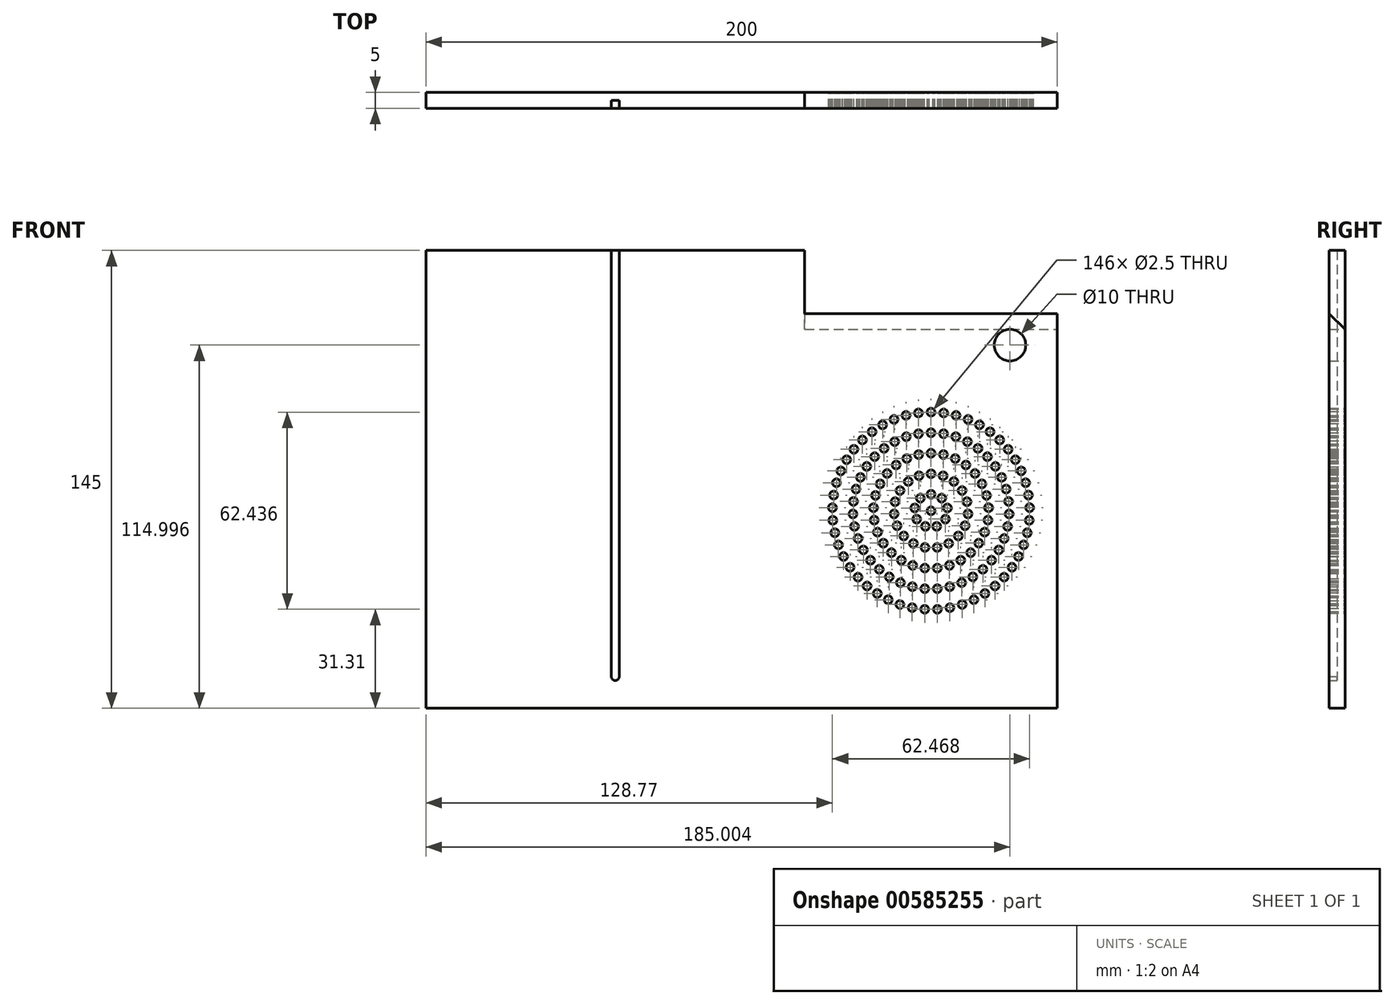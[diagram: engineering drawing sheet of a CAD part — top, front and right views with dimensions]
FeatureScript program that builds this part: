
annotation { "Feature Type Name" : "Feature", "Feature Type Description" : "" }
export const myFeature = defineFeature(function(context is Context, id is Id, definition is map)
    precondition{}
    {
        {
            var Q0;
            Q0=qCreatedBy(makeId("Front.planeOp"),FACE);
            var sketch = newSketch(context, id + "F0", { "sketchPlane" : qUnion([Q0])});
            skLineSegment(sketch, "E0", {"start": v(-78.93, 75.1) * mm, "end": v(1.07, 75.1) * mm});
            skLineSegment(sketch, "E1", {"start": v(1.07, 75.1) * mm, "end": v(1.07, -49.9) * mm});
            skLineSegment(sketch, "E2", {"start": v(-78.93, 75.1) * mm, "end": v(-78.93, 95.1) * mm});
            skLineSegment(sketch, "E3", {"start": v(-198.93, 95.1) * mm, "end": v(-198.93, -49.9) * mm});
            skLineSegment(sketch, "E4", {"start": v(-198.93, -49.9) * mm, "end": v(1.07, -49.9) * mm});
            skLineSegment(sketch, "E5", {"start": v(-198.93, 95.1) * mm, "end": v(-140.18, 95.1) * mm});
            skLineSegment(sketch, "E6", {"start": v(-140.18, 95.1) * mm, "end": v(-137.68, 95.1) * mm});
            skLineSegment(sketch, "E7", {"start": v(-137.68, 95.1) * mm, "end": v(-78.93, 95.1) * mm});
            skLineSegment(sketch, "E8", {"start": v(-140.18, 95.1) * mm, "end": v(-140.18, -39.9) * mm});
            skLineSegment(sketch, "E9", {"start": v(-137.68, 95.1) * mm, "end": v(-137.68, -39.9) * mm});
            skArc(sketch, "E10", {"start": v(-140.18, -39.9) * mm, "mid": v(-138.88, -41.14) * mm, "end": v(-137.68, -39.8) * mm});
            skLineSegment(sketch, "E11", {"start": v(-78.93, 75.1) * mm, "end": v(-78.93, -49.9) * mm});
            skPoint(sketch, "E12.endSnap0", {"position": v(-78.93, 12.6) * mm});
            skCircle(sketch, "E13", {"center": v(-38.93, 12.6) * mm, "radius": 35 * mm});
            skCircle(sketch, "E14", {"center": v(-38.93, 17.86) * mm, "radius": 1.25 * mm});
            skCircle(sketch, "E15.1.0", {"center": v(-35.55, 16.63) * mm, "radius": 1.25 * mm});
            skCircle(sketch, "E15.2.0", {"center": v(-33.76, 13.52) * mm, "radius": 1.25 * mm});
            skCircle(sketch, "E15.3.0", {"center": v(-34.38, 9.98) * mm, "radius": 1.25 * mm});
            skCircle(sketch, "E15.4.0", {"center": v(-37.13, 7.67) * mm, "radius": 1.25 * mm});
            skCircle(sketch, "E15.5.0", {"center": v(-40.72, 7.67) * mm, "radius": 1.25 * mm});
            skCircle(sketch, "E15.6.0", {"center": v(-43.47, 9.98) * mm, "radius": 1.25 * mm});
            skCircle(sketch, "E15.7.0", {"center": v(-44.1, 13.52) * mm, "radius": 1.25 * mm});
            skCircle(sketch, "E15.8.0", {"center": v(-42.3, 16.63) * mm, "radius": 1.25 * mm});
            skLineSegment(sketch, "E15.anchor1", {"start": v(-38.93, 12.6) * mm, "end": v(-38.93, 17.86) * mm, "construction": true});
            skLineSegment(sketch, "E15.anchor2", {"start": v(-38.93, 12.6) * mm, "end": v(-38.93, 17.86) * mm, "construction": true});
            skCircle(sketch, "E16", {"center": v(-38.93, 24.36) * mm, "radius": 1.25 * mm});
            skCircle(sketch, "E17.1.0", {"center": v(-35.11, 23.72) * mm, "radius": 1.25 * mm});
            skCircle(sketch, "E17.2.0", {"center": v(-31.7, 21.88) * mm, "radius": 1.25 * mm});
            skCircle(sketch, "E17.3.0", {"center": v(-29.09, 19.03) * mm, "radius": 1.25 * mm});
            skCircle(sketch, "E17.4.0", {"center": v(-27.54, 15.5) * mm, "radius": 1.25 * mm});
            skCircle(sketch, "E17.5.0", {"center": v(-27.22, 11.64) * mm, "radius": 1.25 * mm});
            skCircle(sketch, "E17.6.0", {"center": v(-28.17, 7.89) * mm, "radius": 1.25 * mm});
            skCircle(sketch, "E17.7.0", {"center": v(-30.28, 4.65) * mm, "radius": 1.25 * mm});
            skCircle(sketch, "E17.8.0", {"center": v(-33.33, 2.27) * mm, "radius": 1.25 * mm});
            skCircle(sketch, "E17.9.0", {"center": v(-37, 1.02) * mm, "radius": 1.25 * mm});
            skLineSegment(sketch, "E17.anchor1", {"start": v(-38.93, 12.6) * mm, "end": v(-38.93, 24.36) * mm, "construction": true});
            skLineSegment(sketch, "E17.anchor2", {"start": v(-38.93, 12.6) * mm, "end": v(-38.93, 24.36) * mm, "construction": true});
            skCircle(sketch, "E18", {"center": v(-38.93, 30.86) * mm, "radius": 1.25 * mm});
            skCircle(sketch, "E19.1.0", {"center": v(-35, 30.43) * mm, "radius": 1.25 * mm});
            skCircle(sketch, "E19.2.0", {"center": v(-31.26, 29.17) * mm, "radius": 1.25 * mm});
            skCircle(sketch, "E19.3.0", {"center": v(-27.88, 27.13) * mm, "radius": 1.25 * mm});
            skCircle(sketch, "E19.4.0", {"center": v(-25.02, 24.42) * mm, "radius": 1.25 * mm});
            skCircle(sketch, "E19.5.0", {"center": v(-22.8, 21.15) * mm, "radius": 1.25 * mm});
            skCircle(sketch, "E19.6.0", {"center": v(-21.34, 17.49) * mm, "radius": 1.25 * mm});
            skCircle(sketch, "E19.7.0", {"center": v(-20.7, 13.6) * mm, "radius": 1.25 * mm});
            skCircle(sketch, "E19.8.0", {"center": v(-20.92, 9.65) * mm, "radius": 1.25 * mm});
            skCircle(sketch, "E19.9.0", {"center": v(-21.97, 5.85) * mm, "radius": 1.25 * mm});
            skLineSegment(sketch, "E19.anchor1", {"start": v(-38.93, 12.6) * mm, "end": v(-38.93, 30.86) * mm, "construction": true});
            skLineSegment(sketch, "E19.anchor2", {"start": v(-38.93, 12.6) * mm, "end": v(-38.93, 30.86) * mm, "construction": true});
            skCircle(sketch, "E20", {"center": v(-38.93, 37.36) * mm, "radius": 1.25 * mm});
            skCircle(sketch, "E21.1.0", {"center": v(-34.96, 37.04) * mm, "radius": 1.25 * mm});
            skCircle(sketch, "E21.2.0", {"center": v(-31.09, 36.08) * mm, "radius": 1.25 * mm});
            skCircle(sketch, "E21.3.0", {"center": v(-27.42, 34.52) * mm, "radius": 1.25 * mm});
            skCircle(sketch, "E21.4.0", {"center": v(-24.06, 32.4) * mm, "radius": 1.25 * mm});
            skCircle(sketch, "E21.5.0", {"center": v(-21.08, 29.75) * mm, "radius": 1.25 * mm});
            skCircle(sketch, "E21.6.0", {"center": v(-18.56, 26.67) * mm, "radius": 1.25 * mm});
            skCircle(sketch, "E21.7.0", {"center": v(-16.57, 23.22) * mm, "radius": 1.25 * mm});
            skCircle(sketch, "E21.8.0", {"center": v(-15.15, 19.5) * mm, "radius": 1.25 * mm});
            skCircle(sketch, "E21.9.0", {"center": v(-14.36, 15.59) * mm, "radius": 1.25 * mm});
            skLineSegment(sketch, "E21.anchor1", {"start": v(-38.93, 12.6) * mm, "end": v(-38.93, 37.36) * mm, "construction": true});
            skLineSegment(sketch, "E21.anchor2", {"start": v(-38.93, 12.6) * mm, "end": v(-38.93, 37.36) * mm, "construction": true});
            skCircle(sketch, "E22.1.10.0", {"center": v(-40.86, 1.02) * mm, "radius": 1.25 * mm});
            skCircle(sketch, "E22.1.11.0", {"center": v(-44.52, 2.27) * mm, "radius": 1.25 * mm});
            skCircle(sketch, "E22.1.12.0", {"center": v(-47.57, 4.65) * mm, "radius": 1.25 * mm});
            skCircle(sketch, "E22.1.13.0", {"center": v(-49.69, 7.89) * mm, "radius": 1.25 * mm});
            skCircle(sketch, "E22.1.14.0", {"center": v(-50.64, 11.64) * mm, "radius": 1.25 * mm});
            skCircle(sketch, "E22.1.15.0", {"center": v(-50.32, 15.5) * mm, "radius": 1.25 * mm});
            skCircle(sketch, "E22.1.16.0", {"center": v(-48.76, 19.03) * mm, "radius": 1.25 * mm});
            skCircle(sketch, "E22.1.17.0", {"center": v(-46.14, 21.88) * mm, "radius": 1.25 * mm});
            skCircle(sketch, "E22.1.18.0", {"center": v(-42.74, 23.72) * mm, "radius": 1.25 * mm});
            skCircle(sketch, "E23.1.10.0", {"center": v(-23.82, 2.36) * mm, "radius": 1.25 * mm});
            skCircle(sketch, "E23.1.11.0", {"center": v(-26.38, -0.64) * mm, "radius": 1.25 * mm});
            skCircle(sketch, "E23.1.12.0", {"center": v(-29.52, -3.03) * mm, "radius": 1.25 * mm});
            skCircle(sketch, "E23.1.13.0", {"center": v(-33.1, -4.69) * mm, "radius": 1.25 * mm});
            skCircle(sketch, "E23.1.14.0", {"center": v(-36.95, -5.54) * mm, "radius": 1.25 * mm});
            skCircle(sketch, "E23.1.15.0", {"center": v(-40.9, -5.54) * mm, "radius": 1.25 * mm});
            skCircle(sketch, "E23.1.16.0", {"center": v(-44.75, -4.69) * mm, "radius": 1.25 * mm});
            skCircle(sketch, "E23.1.17.0", {"center": v(-48.34, -3.03) * mm, "radius": 1.25 * mm});
            skCircle(sketch, "E23.1.18.0", {"center": v(-51.48, -0.64) * mm, "radius": 1.25 * mm});
            skCircle(sketch, "E23.1.19.0", {"center": v(-54.03, 2.36) * mm, "radius": 1.25 * mm});
            skCircle(sketch, "E23.1.20.0", {"center": v(-55.88, 5.85) * mm, "radius": 1.25 * mm});
            skCircle(sketch, "E23.1.21.0", {"center": v(-56.94, 9.65) * mm, "radius": 1.25 * mm});
            skCircle(sketch, "E23.1.22.0", {"center": v(-57.15, 13.6) * mm, "radius": 1.25 * mm});
            skCircle(sketch, "E23.1.23.0", {"center": v(-56.51, 17.49) * mm, "radius": 1.25 * mm});
            skCircle(sketch, "E23.1.24.0", {"center": v(-55.05, 21.15) * mm, "radius": 1.25 * mm});
            skCircle(sketch, "E23.1.25.0", {"center": v(-52.84, 24.42) * mm, "radius": 1.25 * mm});
            skCircle(sketch, "E23.1.26.0", {"center": v(-49.97, 27.13) * mm, "radius": 1.25 * mm});
            skCircle(sketch, "E23.1.27.0", {"center": v(-46.59, 29.17) * mm, "radius": 1.25 * mm});
            skCircle(sketch, "E23.1.28.0", {"center": v(-42.85, 30.43) * mm, "radius": 1.25 * mm});
            skCircle(sketch, "E24.1.10.0", {"center": v(-14.2, 11.6) * mm, "radius": 1.25 * mm});
            skCircle(sketch, "E24.1.11.0", {"center": v(-14.68, 7.66) * mm, "radius": 1.25 * mm});
            skCircle(sketch, "E24.1.12.0", {"center": v(-15.78, 3.83) * mm, "radius": 1.25 * mm});
            skCircle(sketch, "E24.1.13.0", {"center": v(-17.5, 0.23) * mm, "radius": 1.25 * mm});
            skCircle(sketch, "E24.1.14.0", {"center": v(-19.75, -3.05) * mm, "radius": 1.25 * mm});
            skCircle(sketch, "E24.1.15.0", {"center": v(-22.51, -5.92) * mm, "radius": 1.25 * mm});
            skCircle(sketch, "E24.1.16.0", {"center": v(-25.7, -8.31) * mm, "radius": 1.25 * mm});
            skCircle(sketch, "E24.1.17.0", {"center": v(-29.23, -10.16) * mm, "radius": 1.25 * mm});
            skCircle(sketch, "E24.1.18.0", {"center": v(-33, -11.43) * mm, "radius": 1.25 * mm});
            skCircle(sketch, "E24.1.19.0", {"center": v(-36.93, -12.06) * mm, "radius": 1.25 * mm});
            skCircle(sketch, "E24.1.20.0", {"center": v(-40.92, -12.06) * mm, "radius": 1.25 * mm});
            skCircle(sketch, "E24.1.21.0", {"center": v(-44.85, -11.43) * mm, "radius": 1.25 * mm});
            skCircle(sketch, "E24.1.22.0", {"center": v(-48.63, -10.16) * mm, "radius": 1.25 * mm});
            skCircle(sketch, "E24.1.23.0", {"center": v(-52.15, -8.31) * mm, "radius": 1.25 * mm});
            skCircle(sketch, "E24.1.24.0", {"center": v(-55.34, -5.92) * mm, "radius": 1.25 * mm});
            skCircle(sketch, "E24.1.25.0", {"center": v(-58.1, -3.05) * mm, "radius": 1.25 * mm});
            skCircle(sketch, "E24.1.26.0", {"center": v(-60.36, 0.23) * mm, "radius": 1.25 * mm});
            skCircle(sketch, "E24.1.27.0", {"center": v(-62.07, 3.83) * mm, "radius": 1.25 * mm});
            skCircle(sketch, "E24.1.28.0", {"center": v(-63.18, 7.66) * mm, "radius": 1.25 * mm});
            skCircle(sketch, "E24.1.29.0", {"center": v(-63.66, 11.6) * mm, "radius": 1.25 * mm});
            skCircle(sketch, "E24.1.30.0", {"center": v(-63.5, 15.59) * mm, "radius": 1.25 * mm});
            skCircle(sketch, "E24.1.31.0", {"center": v(-62.7, 19.5) * mm, "radius": 1.25 * mm});
            skCircle(sketch, "E24.1.32.0", {"center": v(-61.29, 23.22) * mm, "radius": 1.25 * mm});
            skCircle(sketch, "E24.1.33.0", {"center": v(-59.3, 26.67) * mm, "radius": 1.25 * mm});
            skCircle(sketch, "E24.1.34.0", {"center": v(-56.78, 29.75) * mm, "radius": 1.25 * mm});
            skCircle(sketch, "E24.1.35.0", {"center": v(-53.8, 32.4) * mm, "radius": 1.25 * mm});
            skCircle(sketch, "E24.1.36.0", {"center": v(-50.43, 34.52) * mm, "radius": 1.25 * mm});
            skCircle(sketch, "E24.1.37.0", {"center": v(-46.76, 36.08) * mm, "radius": 1.25 * mm});
            skCircle(sketch, "E24.1.38.0", {"center": v(-42.9, 37.04) * mm, "radius": 1.25 * mm});
            skCircle(sketch, "E25", {"center": v(-13.93, 65.1) * mm, "radius": 5 * mm});
            skCircle(sketch, "E26", {"center": v(-38.93, 43.86) * mm, "radius": 1.25 * mm});
            skCircle(sketch, "E27.1.0", {"center": v(-34.93, 43.6) * mm, "radius": 1.25 * mm});
            skCircle(sketch, "E27.2.0", {"center": v(-31, 42.83) * mm, "radius": 1.25 * mm});
            skCircle(sketch, "E27.3.0", {"center": v(-27.2, 41.57) * mm, "radius": 1.25 * mm});
            skCircle(sketch, "E27.4.0", {"center": v(-23.6, 39.83) * mm, "radius": 1.25 * mm});
            skCircle(sketch, "E27.5.0", {"center": v(-20.24, 37.65) * mm, "radius": 1.25 * mm});
            skCircle(sketch, "E27.6.0", {"center": v(-17.19, 35.05) * mm, "radius": 1.25 * mm});
            skCircle(sketch, "E27.7.0", {"center": v(-14.5, 32.09) * mm, "radius": 1.25 * mm});
            skCircle(sketch, "E27.8.0", {"center": v(-12.2, 28.8) * mm, "radius": 1.25 * mm});
            skCircle(sketch, "E27.9.0", {"center": v(-10.35, 25.26) * mm, "radius": 1.25 * mm});
            skLineSegment(sketch, "E27.anchor1", {"start": v(-38.93, 12.6) * mm, "end": v(-38.93, 43.86) * mm, "construction": true});
            skLineSegment(sketch, "E27.anchor2", {"start": v(-38.93, 12.6) * mm, "end": v(-38.93, 43.86) * mm, "construction": true});
            skCircle(sketch, "E28.1.10.0", {"center": v(-8.97, 21.5) * mm, "radius": 1.25 * mm});
            skCircle(sketch, "E28.1.11.0", {"center": v(-8.08, 17.6) * mm, "radius": 1.25 * mm});
            skCircle(sketch, "E28.1.12.0", {"center": v(-7.7, 13.6) * mm, "radius": 1.25 * mm});
            skCircle(sketch, "E28.1.13.0", {"center": v(-7.82, 9.6) * mm, "radius": 1.25 * mm});
            skCircle(sketch, "E28.1.14.0", {"center": v(-8.46, 5.65) * mm, "radius": 1.25 * mm});
            skCircle(sketch, "E28.1.15.0", {"center": v(-9.6, 1.81) * mm, "radius": 1.25 * mm});
            skCircle(sketch, "E28.1.16.0", {"center": v(-11.22, -1.85) * mm, "radius": 1.25 * mm});
            skCircle(sketch, "E28.1.17.0", {"center": v(-13.3, -5.27) * mm, "radius": 1.25 * mm});
            skCircle(sketch, "E28.1.18.0", {"center": v(-15.8, -8.4) * mm, "radius": 1.25 * mm});
            skCircle(sketch, "E28.1.19.0", {"center": v(-18.67, -11.19) * mm, "radius": 1.25 * mm});
            skCircle(sketch, "E28.1.20.0", {"center": v(-21.88, -13.58) * mm, "radius": 1.25 * mm});
            skCircle(sketch, "E28.1.21.0", {"center": v(-25.37, -15.55) * mm, "radius": 1.25 * mm});
            skCircle(sketch, "E28.1.22.0", {"center": v(-29.08, -17.05) * mm, "radius": 1.25 * mm});
            skCircle(sketch, "E28.1.23.0", {"center": v(-32.95, -18.07) * mm, "radius": 1.25 * mm});
            skCircle(sketch, "E28.1.24.0", {"center": v(-36.92, -18.58) * mm, "radius": 1.25 * mm});
            skCircle(sketch, "E28.1.25.0", {"center": v(-40.93, -18.58) * mm, "radius": 1.25 * mm});
            skCircle(sketch, "E28.1.26.0", {"center": v(-44.9, -18.07) * mm, "radius": 1.25 * mm});
            skCircle(sketch, "E28.1.27.0", {"center": v(-48.77, -17.05) * mm, "radius": 1.25 * mm});
            skCircle(sketch, "E28.1.28.0", {"center": v(-52.49, -15.55) * mm, "radius": 1.25 * mm});
            skCircle(sketch, "E28.1.29.0", {"center": v(-55.97, -13.58) * mm, "radius": 1.25 * mm});
            skCircle(sketch, "E28.1.30.0", {"center": v(-59.18, -11.19) * mm, "radius": 1.25 * mm});
            skCircle(sketch, "E28.1.31.0", {"center": v(-62.06, -8.4) * mm, "radius": 1.25 * mm});
            skCircle(sketch, "E28.1.32.0", {"center": v(-64.56, -5.27) * mm, "radius": 1.25 * mm});
            skCircle(sketch, "E28.1.33.0", {"center": v(-66.63, -1.85) * mm, "radius": 1.25 * mm});
            skCircle(sketch, "E28.1.34.0", {"center": v(-68.25, 1.81) * mm, "radius": 1.25 * mm});
            skCircle(sketch, "E28.1.35.0", {"center": v(-69.4, 5.65) * mm, "radius": 1.25 * mm});
            skCircle(sketch, "E28.1.36.0", {"center": v(-70.03, 9.6) * mm, "radius": 1.25 * mm});
            skCircle(sketch, "E28.1.37.0", {"center": v(-70.16, 13.6) * mm, "radius": 1.25 * mm});
            skCircle(sketch, "E28.1.38.0", {"center": v(-69.78, 17.6) * mm, "radius": 1.25 * mm});
            skCircle(sketch, "E28.1.39.0", {"center": v(-68.88, 21.5) * mm, "radius": 1.25 * mm});
            skCircle(sketch, "E28.1.40.0", {"center": v(-67.5, 25.26) * mm, "radius": 1.25 * mm});
            skCircle(sketch, "E28.1.41.0", {"center": v(-65.65, 28.8) * mm, "radius": 1.25 * mm});
            skCircle(sketch, "E28.1.42.0", {"center": v(-63.36, 32.09) * mm, "radius": 1.25 * mm});
            skCircle(sketch, "E28.1.43.0", {"center": v(-60.67, 35.05) * mm, "radius": 1.25 * mm});
            skCircle(sketch, "E28.1.44.0", {"center": v(-57.62, 37.65) * mm, "radius": 1.25 * mm});
            skCircle(sketch, "E28.1.45.0", {"center": v(-54.26, 39.83) * mm, "radius": 1.25 * mm});
            skCircle(sketch, "E28.1.46.0", {"center": v(-50.65, 41.57) * mm, "radius": 1.25 * mm});
            skCircle(sketch, "E28.1.47.0", {"center": v(-46.85, 42.83) * mm, "radius": 1.25 * mm});
            skCircle(sketch, "E28.1.48.0", {"center": v(-42.92, 43.6) * mm, "radius": 1.25 * mm});
            skCircle(sketch, "E29", {"center": v(-38.93, 12.6) * mm, "radius": 1.25 * mm});
            skSolve(sketch);
        }
        {
            var Q0;
            Q0=makeQuery(id+"F0.imprint","IMPRINT",FACE,{"disambiguationData":[TD([[makeQuery(id+"F0.imprint","IMPRINT",EDGE,{"derivedFrom":sQuery(id+"F0.wireOp",EDGE,"E2")}),1.0]])]});
            var Q1;
            Q1=makeQuery(id+"F0.imprint","IMPRINT",FACE,{"disambiguationData":[TD([[makeQuery(id+"F0.imprint","IMPRINT",EDGE,{"derivedFrom":sQuery(id+"F0.wireOp",EDGE,"E0")}),-1.0]])]});
            var Q2;
            Q2=makeQuery(id+"F0.imprint","IMPRINT",FACE,{"disambiguationData":[TD([[makeQuery(id+"F0.imprint","IMPRINT",EDGE,{"derivedFrom":sQuery(id+"F0.wireOp",EDGE,"E13")}),1.0]])]});
            extrude(context, id + "F1", {"entities" : qUnion([Q0, Q1, Q2]), "depth" : 5 * mm, "offsetDistance" : 25 * mm});
        }
        {
            var Q0;
            {var subQ0=sQuery(id+"F0.wireOp",EDGE,"E6");Q0=makeQuery(id+"F0.imprint","IMPRINT",FACE,{"disambiguationData":[TD([[makeQuery(id+"F0.imprint","IMPRINT",EDGE,{"derivedFrom":subQ0}),-1.0]])]});}
            extrude(context, id + "F2", {"entities" : qUnion([Q0]), "operationType" : NewBodyOperationType.ADD, "depth" : 2.5 * mm, "offsetDistance" : 25 * mm});
        }
        {
            var Q0;
            Q0=makeQuery(id+"F1.opExtrude","CAP_EDGE",EDGE,{"disambiguationData":[OSD([sQuery(id+"F0.wireOp",EDGE,"E0")])],"isStart":true});
            chamfer(context, id + "F3", {"entities" : qUnion([Q0]), "chamferType" : ChamferType.OFFSET_ANGLE, "width" : 5 * mm, "oppositeDirection" : false, "angle" : 45 * degree, "tangentPropagation" : true});
        }
    });
